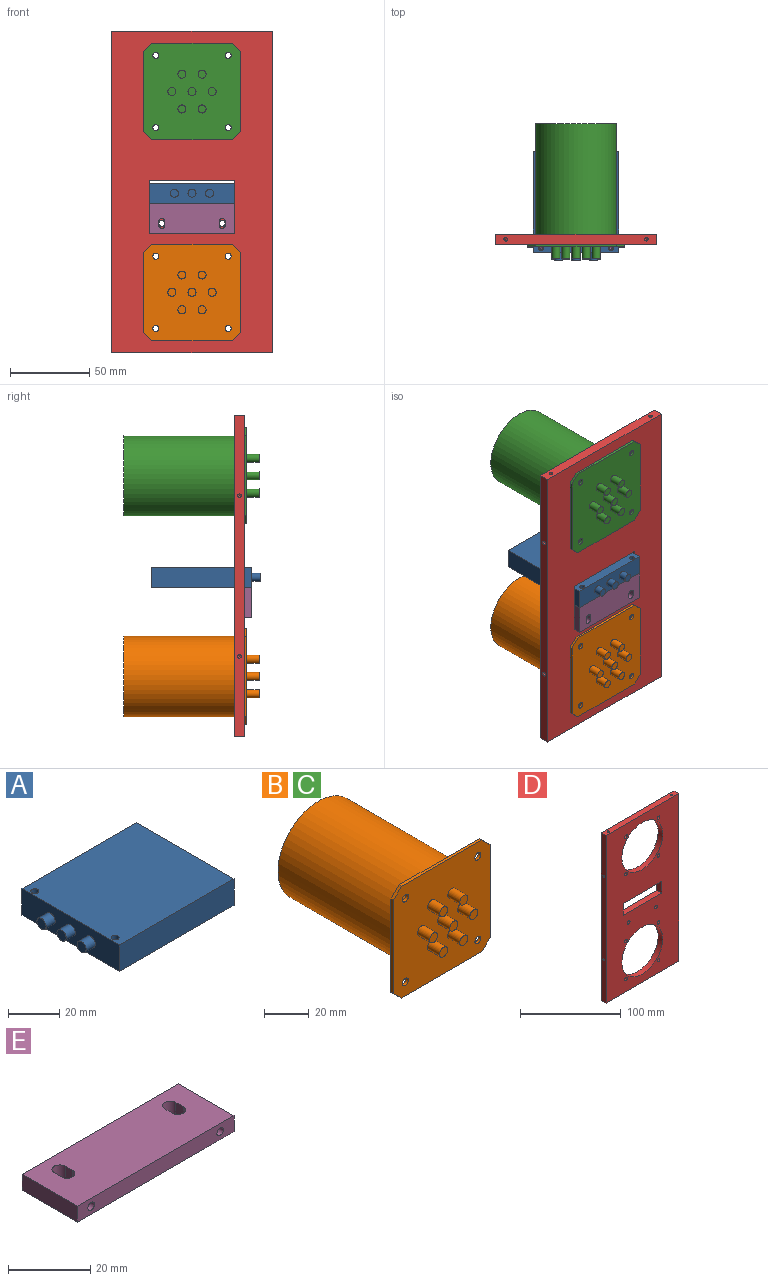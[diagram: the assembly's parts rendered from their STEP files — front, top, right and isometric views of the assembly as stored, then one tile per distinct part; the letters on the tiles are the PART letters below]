
ASSEMBLY  parts=5 mates=4
PART A: 14 faces, bbox 68.6x54x12.7 mm
  f0: plane 63.5x53.98mm, normal (0,0,1), area 3411.6mm2, adj f2,f3,f4,f5,f12,f13
  f1: plane 63.5x53.98mm, normal (0,0,-1), area 3411.6mm2, adj f2,f3,f4,f5,f12,f13
  f2: plane 53.98x12.7mm, normal (-1,0,0), area 624.7mm2, adj f0,f1,f3,f5,f6,f8,f10
  f3: plane 63.5x12.7mm, normal (0,-1,0), area 806.5mm2, adj f0,f1,f2,f4
  f4: plane 53.98x12.7mm, normal (1,0,0), area 685.5mm2, adj f0,f1,f3,f5
  f5: plane 63.5x12.7mm, normal (0,1,0), area 806.5mm2, adj f0,f1,f2,f4
  f6: cylinder r=2.54mm len=5.08mm, axis (1,0,0), area 81.1mm2, adj f2,f7
  f7: plane 5.08x5.08mm, normal (-1,0,0), area 20.3mm2, adj f6
  f8: cylinder r=2.54mm len=5.08mm, axis (1,0,0), area 81.1mm2, adj f2,f9
  f9: plane 5.08x5.08mm, normal (-1,0,0), area 20.3mm2, adj f8
  f10: cylinder r=2.54mm len=5.08mm, axis (1,0,0), area 81.1mm2, adj f2,f11
  f11: plane 5.08x5.08mm, normal (-1,0,0), area 20.3mm2, adj f10
  f12: cylinder r=1.59mm len=12.7mm, axis (0,0,1), area 126.7mm2, adj f0,f1
  f13: cylinder r=1.59mm len=12.7mm, axis (0,0,1), area 126.7mm2, adj f0,f1
PART B: 30 faces, bbox 61x85.4x61 mm
  f0: plane 60.96x60.96mm, normal (0,-1,0), area 3477mm2, adj f4,f5,f6,f7,f8,f9,f10,f11
  f1: plane 60.96x60.96mm, normal (0,1,0), area 1592.1mm2, adj f2,f4,f5,f6,f7,f8,f9,f10
  f2: cylinder r=25.4mm len=76.2mm, axis (0,1,0), area 12161mm2, adj f1,f3
  f3: plane 50.8x50.8mm, normal (0,1,0), area 2026.8mm2, adj f2
  f4: plane 50.8x1.59mm, normal (0,0,1), area 80.6mm2, adj f0,f1,f9,f11
  f5: plane 50.8x1.59mm, normal (-1,0,0), area 80.6mm2, adj f0,f1,f8,f9
  f6: plane 50.8x1.59mm, normal (0,0,-1), area 80.6mm2, adj f0,f1,f8,f10
  f7: plane 50.8x1.59mm, normal (1,0,0), area 80.6mm2, adj f0,f1,f10,f11
  f8: plane 5.08x5.08mm, normal (-0.71,0,-0.71), area 11.4mm2, adj f0,f1,f5,f6
  f9: plane 5.08x5.08mm, normal (-0.71,0,0.71), area 11.4mm2, adj f0,f1,f4,f5
  f10: plane 5.08x5.08mm, normal (0.71,0,-0.71), area 11.4mm2, adj f0,f1,f6,f7
  f11: plane 5.08x5.08mm, normal (0.71,0,0.71), area 11.4mm2, adj f0,f1,f4,f7
  f12: cylinder r=2.54mm len=7.62mm, axis (0,1,0), area 121.6mm2, adj f0,f13
  f13: plane 5.08x5.08mm, normal (0,-1,0), area 20.3mm2, adj f12
  f14: cylinder r=2.54mm len=7.62mm, axis (0,1,0), area 121.6mm2, adj f0,f15
  f15: plane 5.08x5.08mm, normal (0,-1,0), area 20.3mm2, adj f14
  f16: cylinder r=2.54mm len=7.62mm, axis (0,1,0), area 121.6mm2, adj f0,f17
  f17: plane 5.08x5.08mm, normal (0,-1,0), area 20.3mm2, adj f16
  f18: cylinder r=2.54mm len=7.62mm, axis (0,1,0), area 121.6mm2, adj f0,f19
  f19: plane 5.08x5.08mm, normal (0,-1,0), area 20.3mm2, adj f18
  f20: cylinder r=2.54mm len=7.62mm, axis (0,1,0), area 121.6mm2, adj f0,f21
  f21: plane 5.08x5.08mm, normal (0,-1,0), area 20.3mm2, adj f20
  f22: cylinder r=2.54mm len=7.62mm, axis (0,1,0), area 121.6mm2, adj f0,f23
  f23: plane 5.08x5.08mm, normal (0,-1,0), area 20.3mm2, adj f22
  f24: cylinder r=2.54mm len=7.62mm, axis (0,1,0), area 121.6mm2, adj f0,f25
  f25: plane 5.08x5.08mm, normal (0,-1,0), area 20.3mm2, adj f24
  f26: cylinder r=1.91mm len=3.81mm, axis (0,-1,0), area 19mm2, adj f0,f1
  f27: cylinder r=1.91mm len=3.81mm, axis (0,-1,0), area 19mm2, adj f0,f1
  f28: cylinder r=1.91mm len=3.81mm, axis (0,-1,0), area 19mm2, adj f0,f1
  f29: cylinder r=1.91mm len=3.81mm, axis (0,-1,0), area 19mm2, adj f0,f1
PART C: same geometry as B
PART D: 38 faces, bbox 101.6x6.4x203.2 mm
  f0: plane 203.2x101.6mm, normal (0,1,0), area 14629.5mm2, adj f2,f3,f4,f5,f6,f7,f8,f9
  f1: plane 203.2x101.6mm, normal (0,-1,0), area 14629.5mm2, adj f2,f3,f4,f5,f6,f7,f8,f9
  f2: plane 101.6x6.35mm, normal (0,0,-1), area 637.1mm2, adj f0,f1,f20,f21,f35,f37
  f3: plane 101.6x6.35mm, normal (0,0,1), area 637.1mm2, adj f0,f1,f20,f21,f27,f29
  f4: plane 14.29x6.35mm, normal (1,0,0), area 90.7mm2, adj f0,f1,f5,f6
  f5: plane 53.98x6.35mm, normal (0,0,1), area 342.7mm2, adj f0,f1,f4,f7
  f6: plane 53.98x6.35mm, normal (0,0,-1), area 342.7mm2, adj f0,f1,f4,f7
  f7: plane 14.29x6.35mm, normal (-1,0,0), area 90.7mm2, adj f0,f1,f5,f6
  f8: cylinder r=28.57mm len=57.15mm, axis (0,1,0), area 1140.1mm2, adj f0,f1
  f9: cylinder r=28.57mm len=57.15mm, axis (0,1,0), area 1140.1mm2, adj f0,f1
  f10: cylinder r=1.91mm len=6.35mm, axis (0,-1,0), area 76mm2, adj f0,f1
  f11: cylinder r=1.91mm len=6.35mm, axis (0,-1,0), area 76mm2, adj f0,f1
  f12: cylinder r=1.91mm len=6.35mm, axis (0,-1,0), area 76mm2, adj f0,f1
  f13: cylinder r=1.91mm len=6.35mm, axis (0,-1,0), area 76mm2, adj f0,f1
  f14: cylinder r=1.91mm len=6.35mm, axis (0,-1,0), area 76mm2, adj f0,f1
  f15: cylinder r=1.91mm len=6.35mm, axis (0,-1,0), area 76mm2, adj f0,f1
  f16: cylinder r=1.91mm len=6.35mm, axis (0,-1,0), area 76mm2, adj f0,f1
  f17: cylinder r=1.91mm len=6.35mm, axis (0,-1,0), area 76mm2, adj f0,f1
  f18: cylinder r=1.91mm len=6.35mm, axis (0,-1,0), area 76mm2, adj f0,f1
  f19: cylinder r=1.91mm len=6.35mm, axis (0,-1,0), area 76mm2, adj f0,f1
  f20: plane 203.2x6.35mm, normal (1,0,0), area 1282.3mm2, adj f0,f1,f2,f3,f23,f25
  f21: plane 203.2x6.35mm, normal (-1,0,0), area 1282.3mm2, adj f0,f1,f2,f3,f31,f33
  f22: cone r=0mm half-angle=59deg, axis (1,0,0), area 4.7mm2, adj f23
  f23: cylinder r=1.13mm len=5.08mm, axis (1,0,0), area 36.1mm2, adj f20,f22
  f24: cone r=0mm half-angle=59deg, axis (1,0,0), area 4.7mm2, adj f25
  f25: cylinder r=1.13mm len=5.08mm, axis (1,0,0), area 36.1mm2, adj f20,f24
  f26: cone r=0mm half-angle=59deg, axis (0,0,1), area 4.7mm2, adj f27
  f27: cylinder r=1.13mm len=5.08mm, axis (0,0,1), area 36.1mm2, adj f3,f26
  f28: cone r=0mm half-angle=59deg, axis (0,0,1), area 4.7mm2, adj f29
  f29: cylinder r=1.13mm len=5.08mm, axis (0,0,1), area 36.1mm2, adj f3,f28
  f30: cone r=0mm half-angle=59deg, axis (-1,0,0), area 4.7mm2, adj f31
  f31: cylinder r=1.13mm len=5.08mm, axis (-1,0,0), area 36.1mm2, adj f21,f30
  f32: cone r=0mm half-angle=59deg, axis (-1,0,0), area 4.7mm2, adj f33
  f33: cylinder r=1.13mm len=5.08mm, axis (-1,0,0), area 36.1mm2, adj f21,f32
  f34: cone r=0mm half-angle=59deg, axis (0,0,-1), area 4.7mm2, adj f35
  f35: cylinder r=1.13mm len=5.08mm, axis (0,0,-1), area 36.1mm2, adj f2,f34
  f36: cone r=0mm half-angle=59deg, axis (0,0,-1), area 4.7mm2, adj f37
  f37: cylinder r=1.13mm len=5.08mm, axis (0,0,-1), area 36.1mm2, adj f2,f36
PART E: 18 faces, bbox 54x19.1x4.8 mm
  f0: plane 53.98x19.05mm, normal (0,0,1), area 986.1mm2, adj f2,f3,f4,f5,f10,f11,f12,f13
  f1: plane 53.98x19.05mm, normal (0,0,-1), area 986.1mm2, adj f2,f3,f4,f5,f10,f11,f12,f13
  f2: plane 19.05x4.76mm, normal (-1,0,0), area 90.7mm2, adj f0,f1,f3,f5
  f3: plane 53.98x4.76mm, normal (0,-1,0), area 249mm2, adj f0,f1,f2,f4,f7,f9
  f4: plane 19.05x4.76mm, normal (1,0,0), area 90.7mm2, adj f0,f1,f3,f5
  f5: plane 53.98x4.76mm, normal (0,1,0), area 257.1mm2, adj f0,f1,f2,f4
  f6: cone r=0mm half-angle=59deg, axis (0,-1,0), area 4.7mm2, adj f7
  f7: cylinder r=1.13mm len=5.08mm, axis (0,-1,0), area 36.1mm2, adj f3,f6
  f8: cone r=0mm half-angle=59deg, axis (0,-1,0), area 4.7mm2, adj f9
  f9: cylinder r=1.13mm len=5.08mm, axis (0,-1,0), area 36.1mm2, adj f3,f8
  f10: plane 4.76x2.54mm, normal (1,0,0), area 12.1mm2, adj f0,f1,f11,f12
  f11: cylinder r=1.91mm len=4.76mm, axis (0,0,1), area 28.5mm2, adj f0,f1,f10,f13
  f12: cylinder r=1.91mm len=4.76mm, axis (0,0,1), area 28.5mm2, adj f0,f1,f10,f13
  f13: plane 4.76x2.54mm, normal (-1,0,0), area 12.1mm2, adj f0,f1,f11,f12
  f14: cylinder r=1.91mm len=4.76mm, axis (0,0,1), area 28.5mm2, adj f0,f1,f15,f16
  f15: plane 4.76x2.54mm, normal (-1,0,0), area 12.1mm2, adj f0,f1,f14,f17
  f16: plane 4.76x2.54mm, normal (1,0,0), area 12.1mm2, adj f0,f1,f14,f17
  f17: cylinder r=1.91mm len=4.76mm, axis (0,0,1), area 28.5mm2, adj f0,f1,f15,f16
PLACE A rot(axis=(0.71,0.71,0),180deg) t=(-191.4,-151.44,41.67)mm
PLACE B t=(-164.42,-70.48,-27.39)mm
PLACE C t=(-164.42,-70.48,99.61)mm
PLACE D t=(-202.52,-145.09,-65.49)mm
PLACE E rot(axis=(-1,0,0),90deg) t=(-191.4,-151.44,28.97)mm
MATE fastened D.f16 <-> B.f29  axis (0,-1,0) through (-141.56,-146.68,-4.53)mm
MATE fastened E.f0 <-> D.f1  axis (0,1,0) through (-164.42,-146.68,28.97)mm
MATE fastened C.f29 <-> D.f10  axis (0,1,0) through (-141.56,-146.68,122.47)mm
MATE fastened A.f12 <-> E.f8  axis (0,0,-1) through (-186.64,-149.06,28.97)mm
